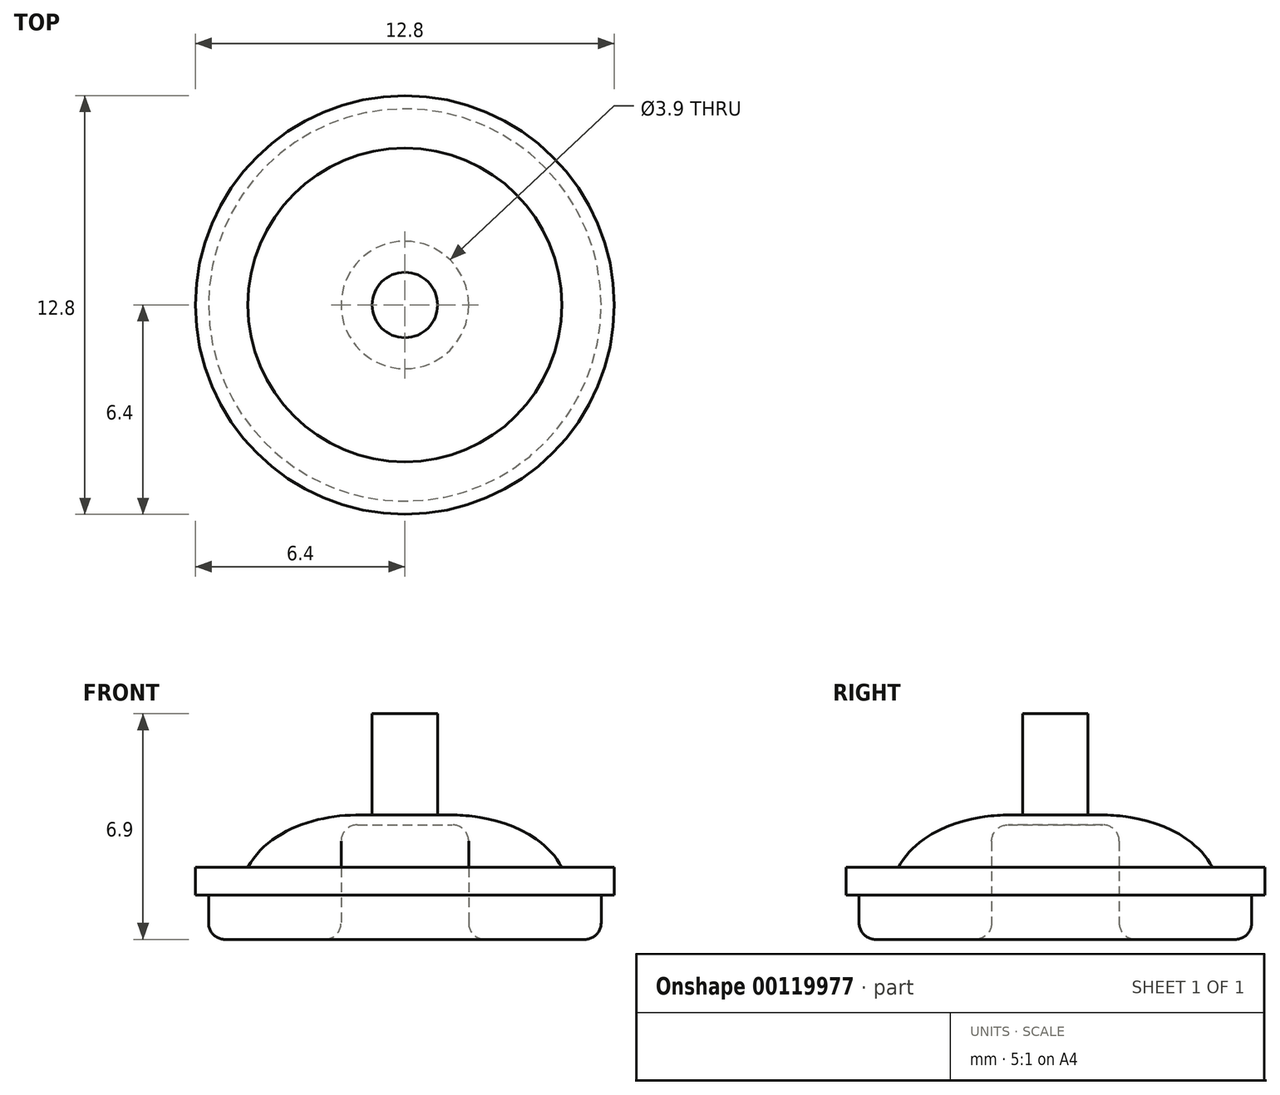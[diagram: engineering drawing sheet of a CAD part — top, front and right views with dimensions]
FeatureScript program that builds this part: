
annotation { "Feature Type Name" : "Feature", "Feature Type Description" : "" }
export const myFeature = defineFeature(function(context is Context, id is Id, definition is map)
    precondition{}
    {
        {
            var Q0;
            Q0=qCreatedBy(makeId("Front.planeOp"),FACE);
            var sketch = newSketch(context, id + "F0", { "sketchPlane" : qUnion([Q0])});
            skLineSegment(sketch, "E0.bottom", {"start": v(0, 0) * mm, "end": v(-6.4, 0) * mm});
            skLineSegment(sketch, "E0.top", {"start": v(0, 0.85) * mm, "end": v(-6.4, 0.85) * mm});
            skLineSegment(sketch, "E0.left", {"start": v(0, 0) * mm, "end": v(0, 0.85) * mm});
            skLineSegment(sketch, "E0.right", {"start": v(-6.4, 0) * mm, "end": v(-6.4, 0.85) * mm});
            skLineSegment(sketch, "E1.bottom", {"start": v(0, 0) * mm, "end": v(-6, 0) * mm});
            skLineSegment(sketch, "E1.top", {"start": v(0, -1.35) * mm, "end": v(-6, -1.35) * mm});
            skLineSegment(sketch, "E1.left", {"start": v(0, 0) * mm, "end": v(0, -1.35) * mm});
            skLineSegment(sketch, "E1.right", {"start": v(-6, 0) * mm, "end": v(-6, -1.35) * mm});
            skLineSegment(sketch, "E2", {"start": v(0, 0.85) * mm, "end": v(0, 2.45) * mm});
            skLineSegment(sketch, "E3", {"start": v(0, 2.45) * mm, "end": v(-1.5, 2.45) * mm});
            skLineSegment(sketch, "E4", {"start": v(0, 0.85) * mm, "end": v(-4.8, 0.85) * mm});
            skFitSpline(sketch, "E5", {"points": [v(-1.5, 2.45) * mm, v(-4.8, 0.85) * mm], "startDerivative": vector(-3.67, 0) * mm, "endDerivative": vector(-1.75, -3.32) * mm});
            skLineSegment(sketch, "E6.bottom", {"start": v(0, 2.45) * mm, "end": v(-1, 2.45) * mm});
            skLineSegment(sketch, "E6.top", {"start": v(0, 5.55) * mm, "end": v(-1, 5.55) * mm});
            skLineSegment(sketch, "E6.left", {"start": v(0, 2.45) * mm, "end": v(0, 5.55) * mm});
            skLineSegment(sketch, "E6.right", {"start": v(-1, 2.45) * mm, "end": v(-1, 5.55) * mm});
            skSolve(sketch);
        }
        {
            var Q0;
            Q0 = qSketchRegion(id + "F0", true);
            var Q1;
            Q1=sQuery(id+"F0.wireOp",EDGE,"E6.left");
            revolve(context, id + "F1", {"entities" : qUnion([Q0]), "axis" : qUnion([Q1]), "revolveType" : RevolveType.FULL});
        }
        {
            var Q0;
            Q0=makeQuery(id+"F1.opRevolve","SWEPT_FACE",FACE,{"disambiguationData":[OSD([sQuery(id+"F0.wireOp",EDGE,"E1.top")])]});
            var Q1;
            Q1=qCreatedBy(makeId("Top.planeOp"),FACE);
            var sketch = newSketch(context, id + "F2", { "sketchPlane" : qUnion([Q0, Q1])});
            skCircle(sketch, "E7", {"center": v(0, 0) * mm, "radius": 1.95 * mm});
            skSolve(sketch);
        }
        {
            var Q0;
            Q0=makeQuery(id+"F2.imprint","IMPRINT",FACE,{"disambiguationData":[TD([[makeQuery(id+"F2.imprint","IMPRINT",EDGE,{"derivedFrom":sQuery(id+"F2.wireOp",EDGE,"E7")}),1.0]])]});
            extrude(context, id + "F3", {"entities" : qUnion([Q0]), "operationType" : NewBodyOperationType.REMOVE, "oppositeDirection" : true, "depth" : 3.5 * mm});
        }
        {
            var Q0;
            Q0=makeQuery(id+"F1.opRevolve","SWEPT_FACE",FACE,{"disambiguationData":[OSD([sQuery(id+"F0.wireOp",EDGE,"E1.top")])]});
            var Q1;
            Q1=makeQuery(id+"F3.boolean.opBoolean","COPY",FACE,{"derivedFrom":makeQuery(id+"F3.opExtrude","CAP_FACE",FACE,{"disambiguationData":[OSD([sQuery(id+"F2.wireOp",EDGE,"E7")])],"isStart":false})});
            fillet(context, id + "F4", {"entities" : qUnion([Q0, Q1]), "radius" : 0.5 * mm, "tangentPropagation" : true, "allowEdgeOverflow" : false});
        }
    });
